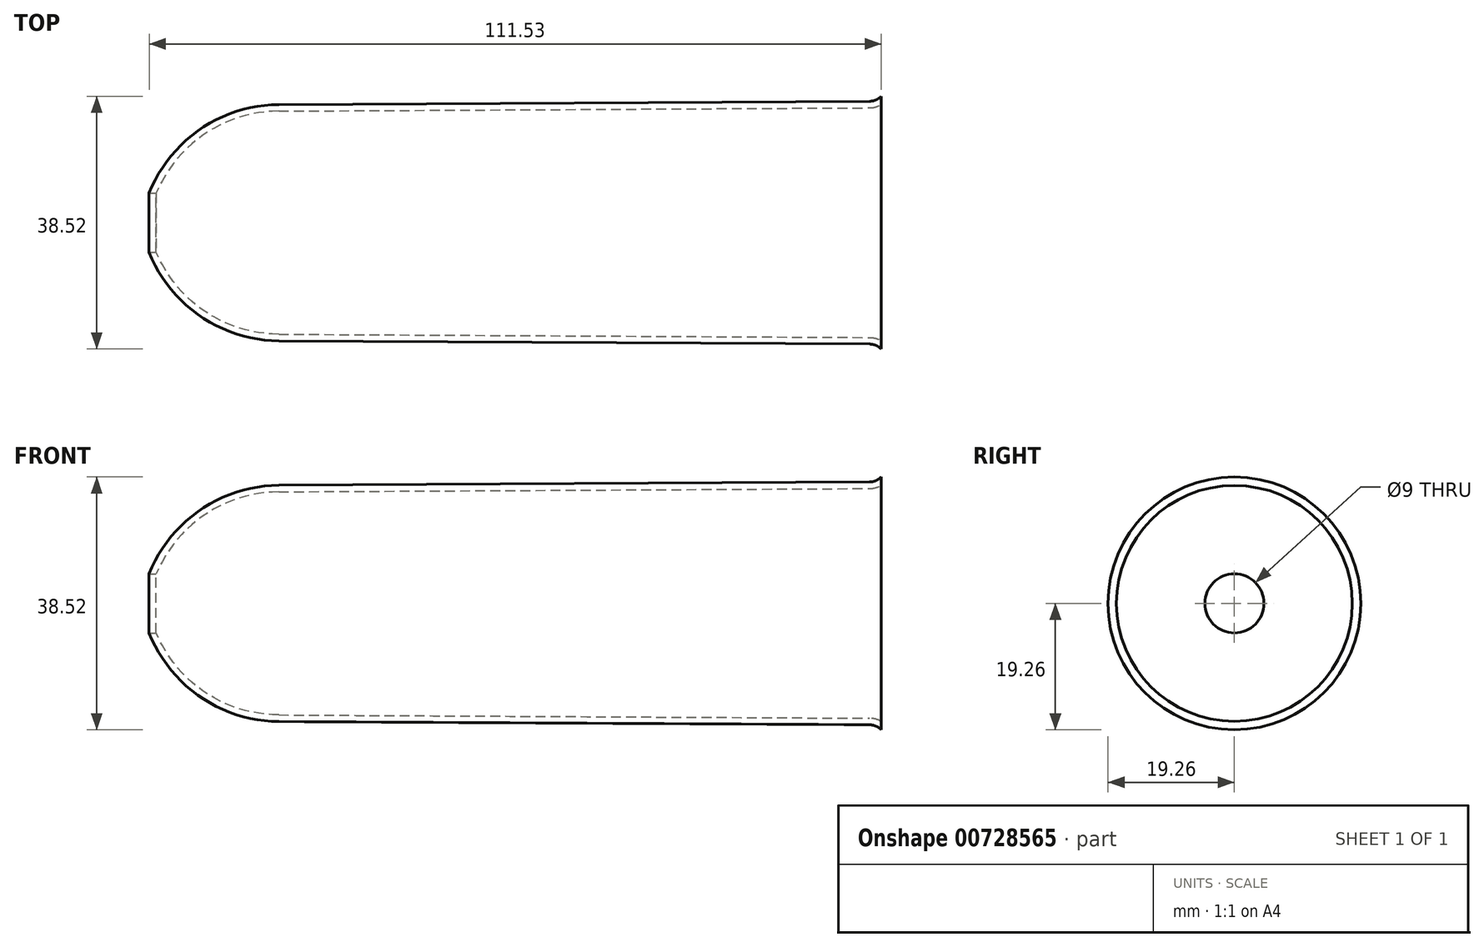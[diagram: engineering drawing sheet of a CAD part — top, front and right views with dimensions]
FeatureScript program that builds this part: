
annotation { "Feature Type Name" : "Feature", "Feature Type Description" : "" }
export const myFeature = defineFeature(function(context is Context, id is Id, definition is map)
    precondition{}
    {
        {
            var Q0;
            Q0=qCreatedBy(makeId("Front.planeOp"),FACE);
            var sketch = newSketch(context, id + "F0", { "sketchPlane" : qUnion([Q0])});
            skLineSegment(sketch, "E0", {"start": v(0, 0) * mm, "end": v(-113.31, 0) * mm, "construction": true});
            skLineSegment(sketch, "E1", {"start": v(0, -17.5) * mm, "end": v(-90, -17) * mm});
            skArc(sketch, "E2", {"start": v(-90, -17) * mm, "mid": v(-103.1, -12.14) * mm, "end": v(-110, 0) * mm});
            skArc(sketch, "E3.0", {"start": v(-90, -18) * mm, "mid": v(-103.8, -12.85) * mm, "end": v(-111.01, 0) * mm});
            skLineSegment(sketch, "E3.1", {"start": v(0, -18.5) * mm, "end": v(-90, -18) * mm});
            skArc(sketch, "E4", {"start": v(0, -17.5) * mm, "mid": v(0.89, -17.62) * mm, "end": v(1.72, -17.97) * mm});
            skArc(sketch, "E5", {"start": v(0, -18.5) * mm, "mid": v(0.95, -18.7) * mm, "end": v(1.76, -19.26) * mm});
            skLineSegment(sketch, "E6", {"start": v(1.76, -19.26) * mm, "end": v(1.72, -17.97) * mm});
            skLineSegment(sketch, "E7", {"start": v(-111.01, 0) * mm, "end": v(-111.01, 0) * mm});
            skLineSegment(sketch, "E8", {"start": v(-111.01, 0) * mm, "end": v(-110, 0) * mm});
            skLineSegment(sketch, "E9.bottom", {"start": v(-113.51, 0) * mm, "end": v(-108.51, 0) * mm});
            skLineSegment(sketch, "E9.top", {"start": v(-113.51, -4.5) * mm, "end": v(-108.51, -4.5) * mm});
            skLineSegment(sketch, "E9.left", {"start": v(-113.51, 0) * mm, "end": v(-113.51, -4.5) * mm});
            skLineSegment(sketch, "E9.right", {"start": v(-108.51, 0) * mm, "end": v(-108.51, -4.5) * mm});
            skSolve(sketch);
        }
        {
            var Q0;
            Q0=makeQuery(id+"F0.imprint","IMPRINT",FACE,{"disambiguationData":[TD([[makeQuery(id+"F0.imprint","IMPRINT",EDGE,{"derivedFrom":sQuery(id+"F0.wireOp",EDGE,"E1")}),1.0]])]});
            var Q1;
            Q1=sQuery(id+"F0.wireOp",EDGE,"E0");
            revolve(context, id + "F1", {"surfaceOperationType" : NewSurfaceOperationType.NEW, "entities" : qUnion([Q0]), "axis" : qUnion([Q1]), "revolveType" : RevolveType.FULL});
        }
    });
